# Revit family: Haworth_Bac_Chair_Two
name_source: partatom
category: Furniture
revit_build: Autodesk Revit 2018 (Build: 20170223_1515(x64)
units: mm (PartAtom-declared; Revit-internal decimal feet)

## family parameters
Always vertical = Yes
Cut with Voids When Loaded = No
OmniClass Number = 23.40.20.00
OmniClass Title = General Furniture and Specialties
Room Calculation Point = No
Shared = No
Work Plane-Based = No

## types (2) — shared parameters
Actual Depth = 19"
Actual Height = 30"
Actual Width = 17 3/4"
Assembly Code = E2020200
Depth = 19 in.
Glide Finish = Haworth _ Paint _ Black
Height = 30 in.
Manufacturer = Haworth
Revision = 1
Seat Height = 17 1/4"
Size = Verify Final Dim. w/ Haworth
URL = http://www.haworth.com
URL - Product = https://www.haworth.com
Warranty = http://www.haworth.com
Width = 17.75 in.

## per-type parameters (varying)
| type | Description | Model | Upholstered Back | Wood Back |
| HCCE-BAC2 - Upholstered Back | Haworth Bac Chair Two - Upholstered Back | HCCE-BAC2 | Yes | No |
| HCCE-BAC2 - Wood Back | Haworth Bac Chair Two - Wood Back | HCCE-BAC2-W | No | Yes |

## geometry (parser evidence)
native form markers: Sweep x2
no freeform markers — native parametric forms only
